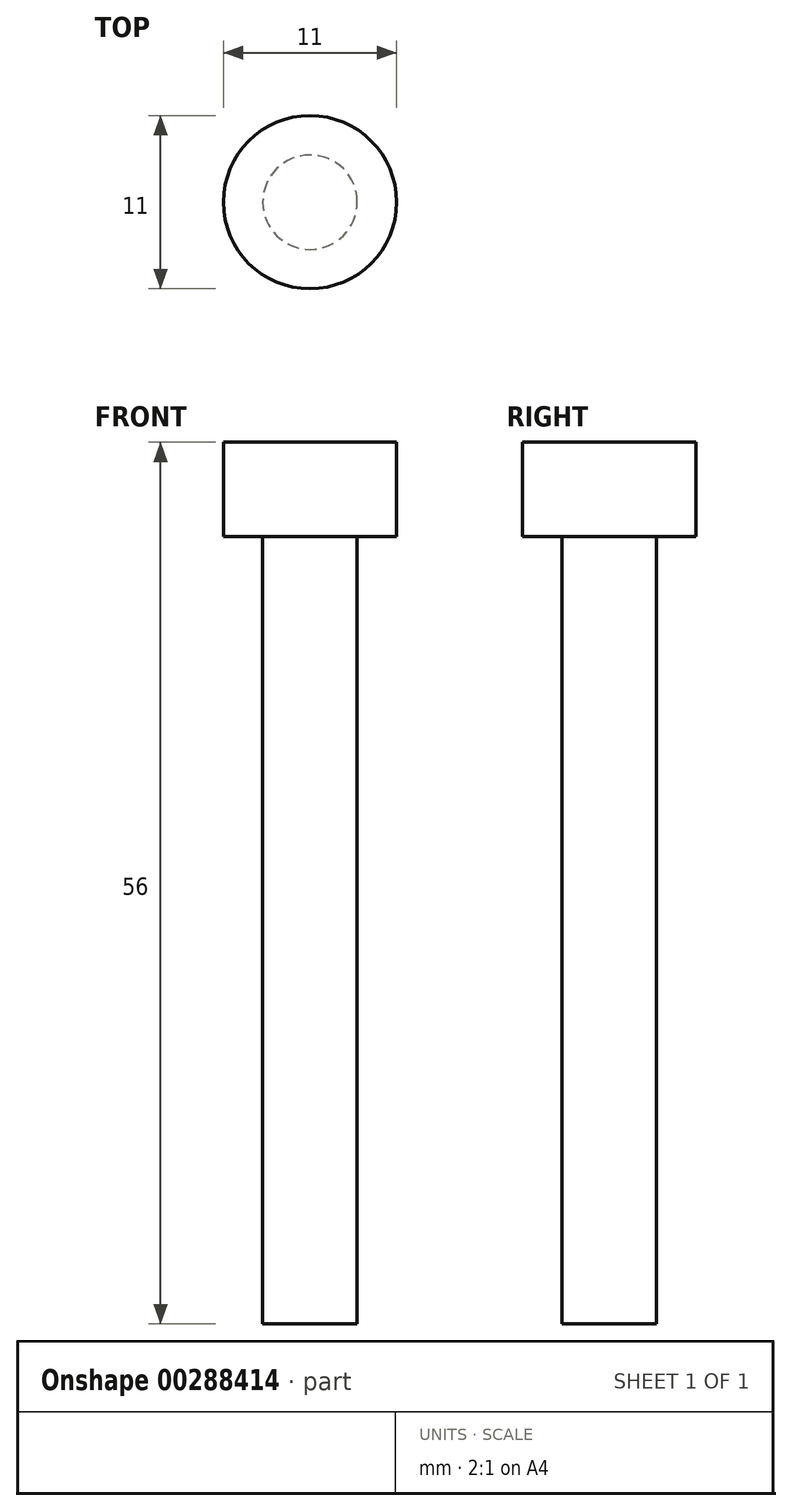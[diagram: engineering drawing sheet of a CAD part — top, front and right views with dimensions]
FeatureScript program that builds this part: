
annotation { "Feature Type Name" : "Feature", "Feature Type Description" : "" }
export const myFeature = defineFeature(function(context is Context, id is Id, definition is map)
    precondition{}
    {
        {
            var Q0;
            Q0=qCreatedBy(makeId("Front.planeOp"),FACE);
            var sketch = newSketch(context, id + "F0", { "sketchPlane" : qUnion([Q0])});
            skLineSegment(sketch, "E0", {"start": v(0, 0) * mm, "end": v(3, 0) * mm});
            skLineSegment(sketch, "E1", {"start": v(5.5, 50) * mm, "end": v(5.5, 56) * mm});
            skLineSegment(sketch, "E2", {"start": v(5.5, 56) * mm, "end": v(0, 56) * mm});
            skLineSegment(sketch, "E3", {"start": v(0, 56) * mm, "end": v(0, 0) * mm});
            skLineSegment(sketch, "E4", {"start": v(3, 0) * mm, "end": v(3, 50) * mm});
            skLineSegment(sketch, "E5", {"start": v(3, 50) * mm, "end": v(5.5, 50) * mm});
            skLineSegment(sketch, "E6", {"start": v(0, 51.38) * mm, "end": v(0, -30.19) * mm, "construction": true});
            skSolve(sketch);
        }
        {
            var Q0;
            Q0=makeQuery(id+"F0.imprint","IMPRINT",FACE,{"disambiguationData":[TD([[makeQuery(id+"F0.imprint","IMPRINT",EDGE,{"derivedFrom":sQuery(id+"F0.wireOp",EDGE,"E0")}),1.0]])]});
            var Q1;
            Q1=sQuery(id+"F0.wireOp",EDGE,"E6");
            revolve(context, id + "F1", {"entities" : qUnion([Q0]), "axis" : qUnion([Q1]), "revolveType" : RevolveType.FULL});
        }
    });
